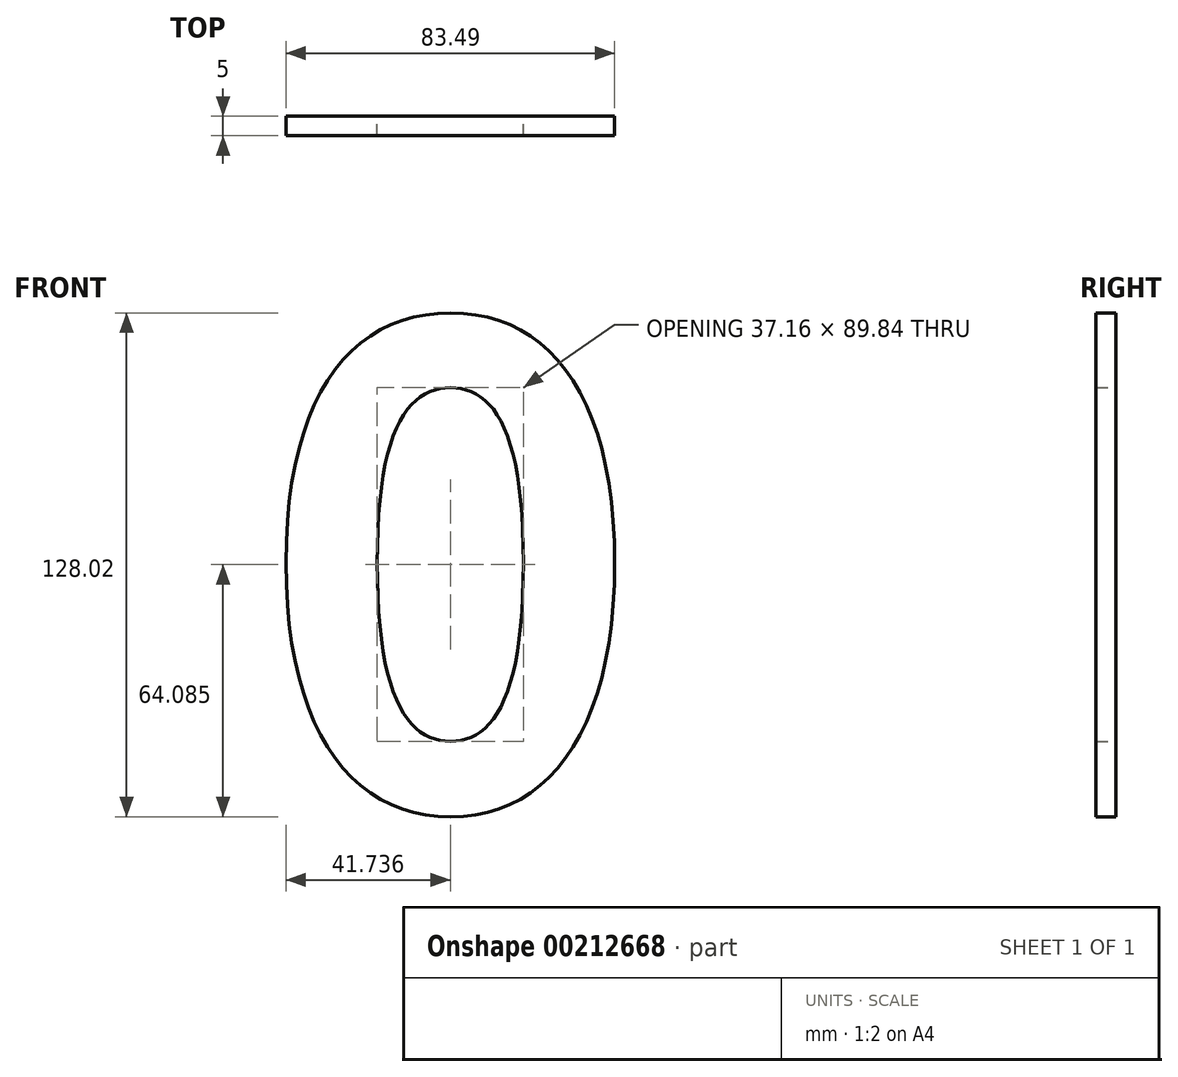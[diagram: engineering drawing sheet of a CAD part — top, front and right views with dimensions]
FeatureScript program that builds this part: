
annotation { "Feature Type Name" : "Feature", "Feature Type Description" : "" }
export const myFeature = defineFeature(function(context is Context, id is Id, definition is map)
    precondition{}
    {
        {
            var Q0;
            Q0=qCreatedBy(makeId("Front.planeOp"),FACE);
            var sketch = newSketch(context, id + "F0", { "sketchPlane" : qUnion([Q0])});
            skText(sketch, "E0", { "text": "0", "fontName": "NotoSansCJKsc-Bold.otf"});
            const initialGuessF0  = {"E0": [-0.06466, -0.06887, 1, 0, 0.12]};
            skSetInitialGuess(sketch, initialGuessF0);
            skSolve(sketch);
        }
        {
            var Q0;
            Q0=makeQuery(id+"F0.imprint","IMPRINT",FACE,{"disambiguationData":[TD([[makeQuery(id+"F0.imprint","IMPRINT",EDGE,{"derivedFrom":sQuery(id+"F0.wireOp",EDGE,"E0.sketch_text.stroke-0")}),1.0]])]});
            extrude(context, id + "F1", {"entities" : qUnion([Q0]), "depth" : 5 * mm});
        }
    });
